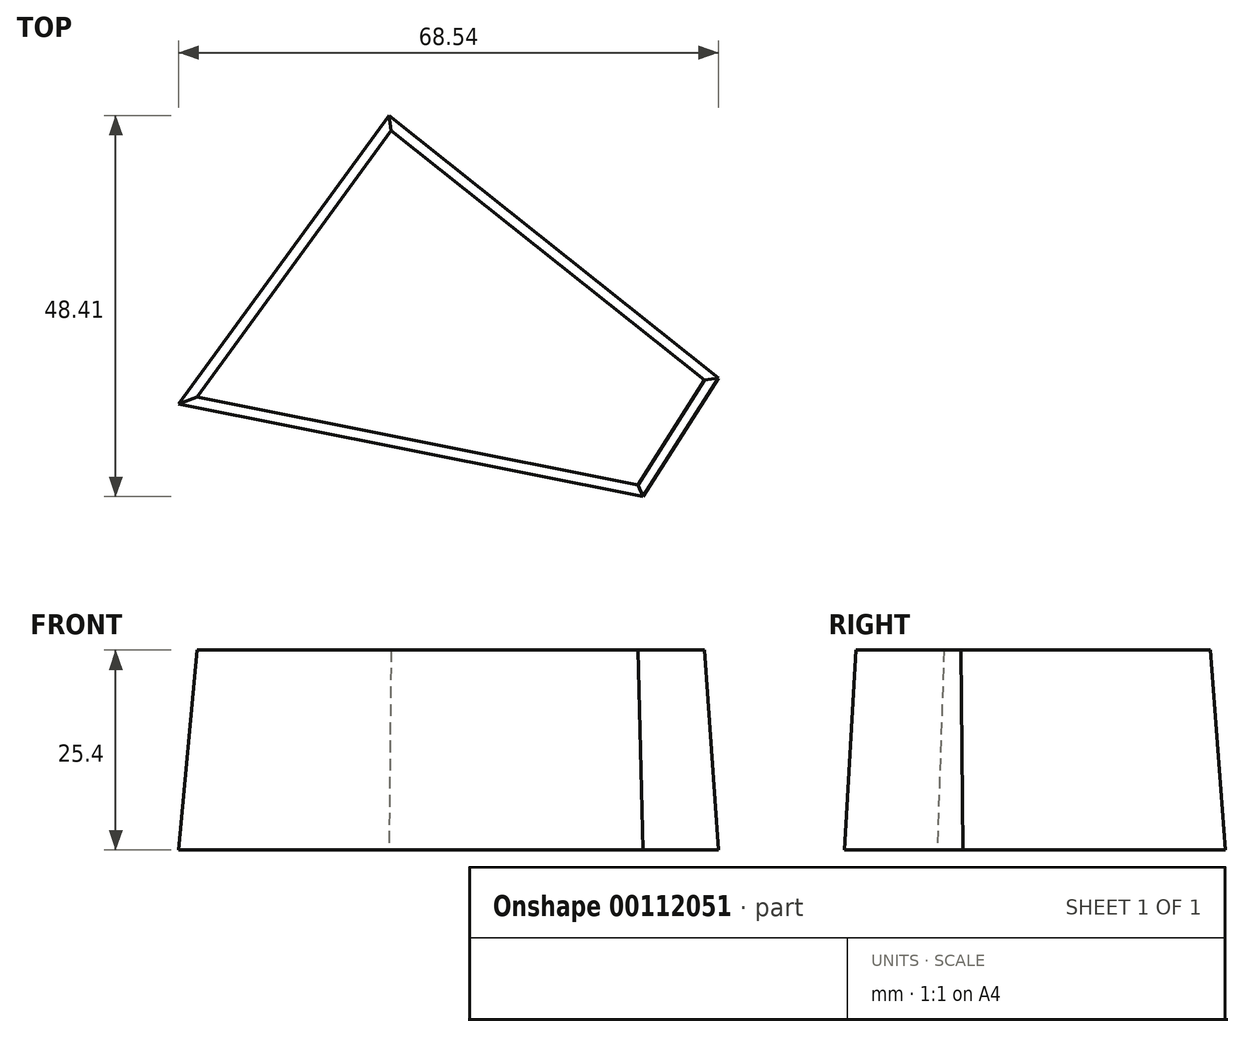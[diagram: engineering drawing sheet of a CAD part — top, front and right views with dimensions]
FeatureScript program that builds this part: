
annotation { "Feature Type Name" : "Feature", "Feature Type Description" : "" }
export const myFeature = defineFeature(function(context is Context, id is Id, definition is map)
    precondition{}
    {
        {
            var Q0;
            Q0=qCreatedBy(makeId("Top.planeOp"),FACE);
            var sketch = newSketch(context, id + "F0", { "sketchPlane" : qUnion([Q0])});
            skLineSegment(sketch, "E0", {"start": v(-80.62, -2.05) * mm, "end": v(-21.67, -13.83) * mm});
            skLineSegment(sketch, "E1", {"start": v(-12.08, 1.26) * mm, "end": v(-53.92, 34.58) * mm});
            skLineSegment(sketch, "E2", {"start": v(-53.92, 34.58) * mm, "end": v(-80.62, -2.05) * mm});
            skLineSegment(sketch, "E3", {"start": v(-12.08, 1.26) * mm, "end": v(-21.67, -13.83) * mm});
            skSolve(sketch);
        }
        {
            var Q0;
            Q0 = qSketchRegion(id + "F0", true);
            extrude(context, id + "F1", {"entities" : qUnion([Q0]), "depth" : 25.4 * mm, "hasDraft" : true, "draftAngle" : 3 * degree, "draftPullDirection" : true});
        }
    });
